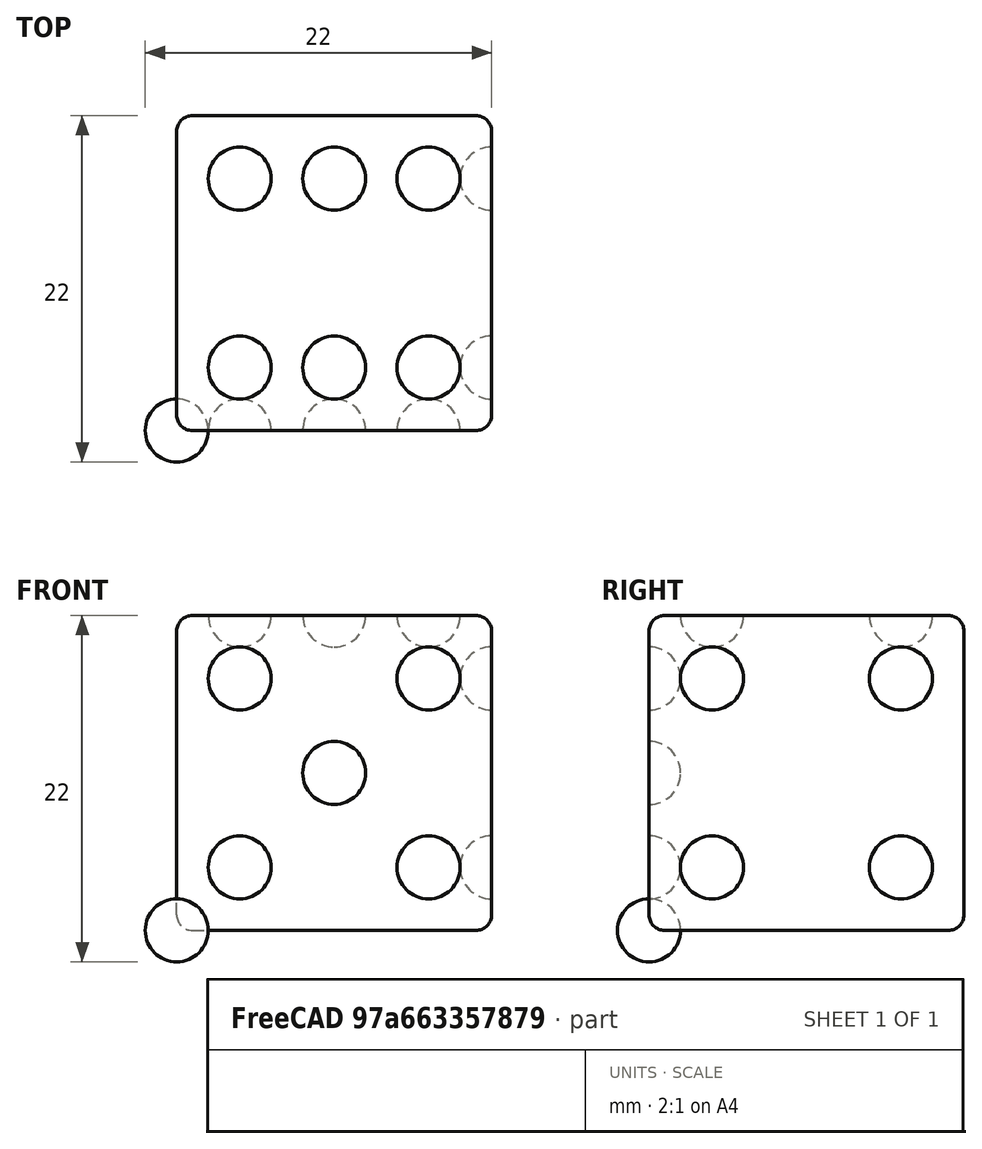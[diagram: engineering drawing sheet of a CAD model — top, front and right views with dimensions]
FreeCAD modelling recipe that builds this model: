
FCSTD DOCUMENT  (FreeCAD 1.0R39319 (Git))
Label: ojt1_t13r02_dado
License: All rights reserved
LicenseURL: https://en.wikipedia.org/wiki/All_rights_reserved
objects: Part::Sphere×3, Part::FeaturePython×3, Part::Cut×3, Part::MultiFuse×1, Part::Box×1, Part::Fillet×1
note: 9 computed .brp shape members not serialized (recipe doc carries the construction recipe); baked Part::Feature solids carry a one-line shape summary decoded from their .brp

FEATURE [Part::Sphere] Sphere  label="Esfera"
  Angle1 = -90
  Angle2 = 90
  Angle3 = 360
  AttacherType = Attacher::AttachEngine3D
  Radius = 2
FEATURE [Part::FeaturePython] Array  label="6"  # Draft array (typed FeaturePython)
  AlwaysSyncPlacement = false
  Angle = 360
  ArrayType = 0
  Axis = (0,0,1)
  Base = -> Sphere
  Center = (0,0,0)
  Count = 6
  ExpandArray = false
  Fuse = false
  IntervalAxis = (0,0,0)
  IntervalX = (6,0,0)
  IntervalY = (0,12,0)
  IntervalZ = (0,0,100)
  NumberCircles = 3
  NumberPolar = 5
  NumberX = 3
  NumberY = 2
  NumberZ = 1
  Placement = pos=(4,4,20) rot=(0,0,1;0rad)
  PlacementList = 6 placements: [(0,0,0),(0,12,0),(6,0,0),(6,12,0),(12,0,0),(12,12,0)]
  RadialDistance = 50
  ScaleList = (6) [(1,1,1),(1,1,1),(1,1,1),(1,1,1),(1,1,1),(1,1,1)]
  Symmetry = 1
  TangentialDistance = 25
FEATURE [Part::Sphere] Sphere001  label="Esfera001"
  Angle1 = -90
  Angle2 = 90
  Angle3 = 360
  AttacherType = Attacher::AttachEngine3D
  Radius = 2
FEATURE [Part::FeaturePython] Array001  label="2342"  # Draft array (typed FeaturePython)
  AlwaysSyncPlacement = false
  Angle = 360
  ArrayType = 0
  Axis = (0,0,1)
  Base = -> Sphere001
  Center = (0,0,0)
  Count = 4
  ExpandArray = false
  Fuse = false
  IntervalAxis = (0,0,0)
  IntervalX = (12,0,0)
  IntervalY = (0,12,0)
  IntervalZ = (0,0,100)
  NumberCircles = 3
  NumberPolar = 5
  NumberX = 2
  NumberY = 2
  NumberZ = 1
  PlacementList = 4 placements: [(0,0,0),(0,12,0),(12,0,0),(12,12,0)]
  RadialDistance = 50
  ScaleList = (4) [(1,1,1),(1,1,1),(1,1,1),(1,1,1)]
  Symmetry = 1
  TangentialDistance = 25
FEATURE [Part::Sphere] Sphere002  label="Esfera002"
  Angle1 = -90
  Angle2 = 90
  Angle3 = 360
  AttacherType = Attacher::AttachEngine3D
  Placement = pos=(6,6,0) rot=(0,0,1;0rad)
  Radius = 2
FEATURE [Part::MultiFuse] Fusion  label="5"
  Placement = pos=(4,0,4) rot=(-0.57735,-0.57735,-0.57735;2.0944rad)
  Refine = true
  Shapes = -> [Sphere002,Array001]
FEATURE [Part::FeaturePython] Array002  label="4"  # Draft array (typed FeaturePython)
  AlwaysSyncPlacement = false
  Angle = 360
  ArrayType = 0
  Axis = (0,0,1)
  Base = -> Sphere001
  Center = (0,0,0)
  Count = 4
  ExpandArray = false
  Fuse = false
  IntervalAxis = (0,0,0)
  IntervalX = (12,0,0)
  IntervalY = (0,12,0)
  IntervalZ = (0,0,100)
  NumberCircles = 3
  NumberPolar = 5
  NumberX = 2
  NumberY = 2
  NumberZ = 1
  Placement = pos=(20,4,4) rot=(0,-1,0;1.5708rad)
  PlacementList = 4 placements: [(0,0,0),(0,12,0),(12,0,0),(12,12,0)]
  RadialDistance = 50
  ScaleList = (4) [(1,1,1),(1,1,1),(1,1,1),(1,1,1)]
  Symmetry = 1
  TangentialDistance = 25
FEATURE [Part::Box] Box  label="Cub"
  AttacherType = Attacher::AttachEngine3D
  Height = 20
  Length = 20
  Width = 20
FEATURE [Part::Fillet] Fillet
  Base = -> Box
  EdgeLinks = -> Box [Edge1,Edge2,Edge3,Edge4,Edge5,Edge6,Edge7,Edge8,Edge9,Edge10,Edge11,Edge12]
  Edges = 12 edges r=1: [Edge1,Edge2,Edge3,Edge4,Edge5,Edge6,Edge7,Edge8,Edge9,Edge10,Edge11,Edge12]
FEATURE [Part::Cut] Cut
  Base = -> Fillet
  Refine = true
  Tool = -> Array002
FEATURE [Part::Cut] Cut001
  Base = -> Cut
  Refine = true
  Tool = -> Fusion
FEATURE [Part::Cut] Cut002
  Base = -> Cut001
  Refine = true
  Tool = -> Array
